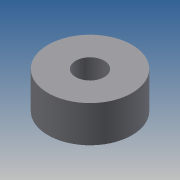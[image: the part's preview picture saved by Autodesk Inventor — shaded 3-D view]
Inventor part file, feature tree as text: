
AUTODESK INVENTOR PART (.ipt)
format: ipt  version: 2013 (Build 170138000, 138)  size: 75,264 bytes
history: native  units: mm
features: extrude x2, sketch x2
ambient origin geometry x8: Origin, YZ Plane, XZ Plane, XY Plane, X Axis, Y Axis, Z Axis, Center Point
bodies: Solid1 (feature_tree)
feature tree (4):
  extrude  "Extrusion1"  Depth=10.9mm TaperAngle=0.0deg
  extrude  "Extrusion2"  Depth=10.96mm TaperAngle=0.0deg
  sketch  "Sketch1"  dims[d0=25.0mm d2=10.9mm d3=0.0mm]
  sketch  "Sketch2"  dims[d4=8.5mm d6=10.96mm d7=0.0mm]
